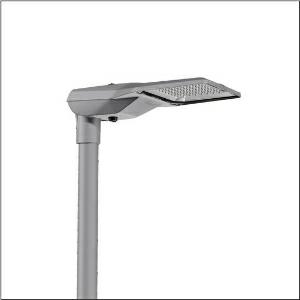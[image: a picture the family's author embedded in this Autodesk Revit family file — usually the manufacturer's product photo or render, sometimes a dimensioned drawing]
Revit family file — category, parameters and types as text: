
# Revit family: streetlight_sl_21_iq_midi___pc-r_5xe3g31y08mb_65a2
name_source: partatom
category: Lighting Fixtures
units: mm (PartAtom-declared; Revit-internal decimal feet)

## family parameters
Cut with Voids When Loaded = No
Host = Face
Light Source = No
Part Type = Normal
Room Calculation Point = No
Round Connector Dimension = Use Diameter
Shared = No

## types (1)
- --- (1 x LED, 17070 lm, 129.3 W, 3000K)
    Apparent Load = 129 VA
    CIE Flux Codes = 38 78 98 100 100
    Color Rendering = 70
    Color Temperature = 3000K
    Default Elevation = 1800 mm
    Description = Streetlight SL 21 iQ midi, mast luminaire, primary light control with lens, of PMMA, primary optical cover: cover, of toughened safety glass, transparent, light distribution: PC-R, light emission: direct distribution, primary light characteristic: asymmetric, right, installation type: post-top, side-entry, LED, High Power LED, rated luminous flux: 17.070lm, luminous efficacy: 132lm/W, light colour: 730, colour temperature: 3000K, control gear: iQ-Street Remote, D4i with power reduction, control: pre-setting: logarithmic dimming characteristic, Street-Remote, Auto-Match, Temp-Guard, Lumen-Switch, Night-Set, Smart-Wire, Light-Fading, Desk-Remote (wireless, voltage-free reading and setting of iQ features in the workshop via application-optimized NFC function/RFID function), optimised constant luminous flux control (CLO 2.0), mains connection: 230..240V, AC, 50/60Hz, start of lifetime: 129W, end of service life: 142W, reduction: 56W, luminaire housing, of diecast aluminium, powder-coated, SITECO metallic grey (DB 702S), corrosivity category C5 high according to DIN EN ISO 12944, please order mast flange separately, inclination adjustable: 0°, 5°, 10°, 15°, sealing non-destructively replaceable, multi-level sealing system, length: 644mm, width: 335mm, height: 110mm, mast flange for spigot size: 42mm (side-entry): 5XC10008XM4, 60/48mm (side-entry/post-top): 5XC10108XM2, 76/60mm (side-entry/post-top): 5XC10108XM1, mounting height: 4..8m, Smart Interface below and above, protection rating (complete): IP66, insulation class (complete): insulation class II (safety insulation), certification: CE, ENEC, ENEC+, VDE, impact resistance: IK10, permissible operating ambient temperature for outdoor applications: -40..+50°C, standard-compliant lighting for roads and squares, packaging unit: 1 piece

Light Distribution: PC-R
    Height = 111 mm
    Lamp = 1 x LED
    Lamp Light Flux = 17070 lm
    Lamp Power = 129.3 W
    Lamp count = 1
    Length = 644 mm
    Luminous efficacy = 132 lm/W
    Manufacturer = Siteco
    ModVariant = No
    Model = 5XE3G31Y08MB
    Number of Poles = 1
    OnlyDefault = Yes
    Power Factor = 1
    Product Name = Streetlight SL 21 iQ midi | PC-R
    Product group = mast luminaire | pylon top
    ProductGroupID = 6100
    Protection Class = Protection class II
    Protection Degree = IP 66
    RLX_Detail_Level = 1
    RLX_Emergency_Light_Flux = 0 lm
    RLX_Emergency_Type = 0
    RLX_Emergency_Type_DB = No
    RlxData = <blob elided: 29685 chars, md5=91c6904c>
    Socket = socket
    Standby Power = 0 W
    System Light Flux = 17070 lm
    System Power = 129 W
    Type Comments = factory setting: luminous flux: 100 % | dim-lin: 254 | 672 mA
    Type Image = l_1004304.jpg
    URL = http://relux.com
    VarID = @adj_071889
    Voltage = 0 V
    Weight = 0.00 kg
    Width = 336 mm

## geometry (parser evidence)
native form markers: Blend x4, Sweep x11
no freeform markers — native parametric forms only
